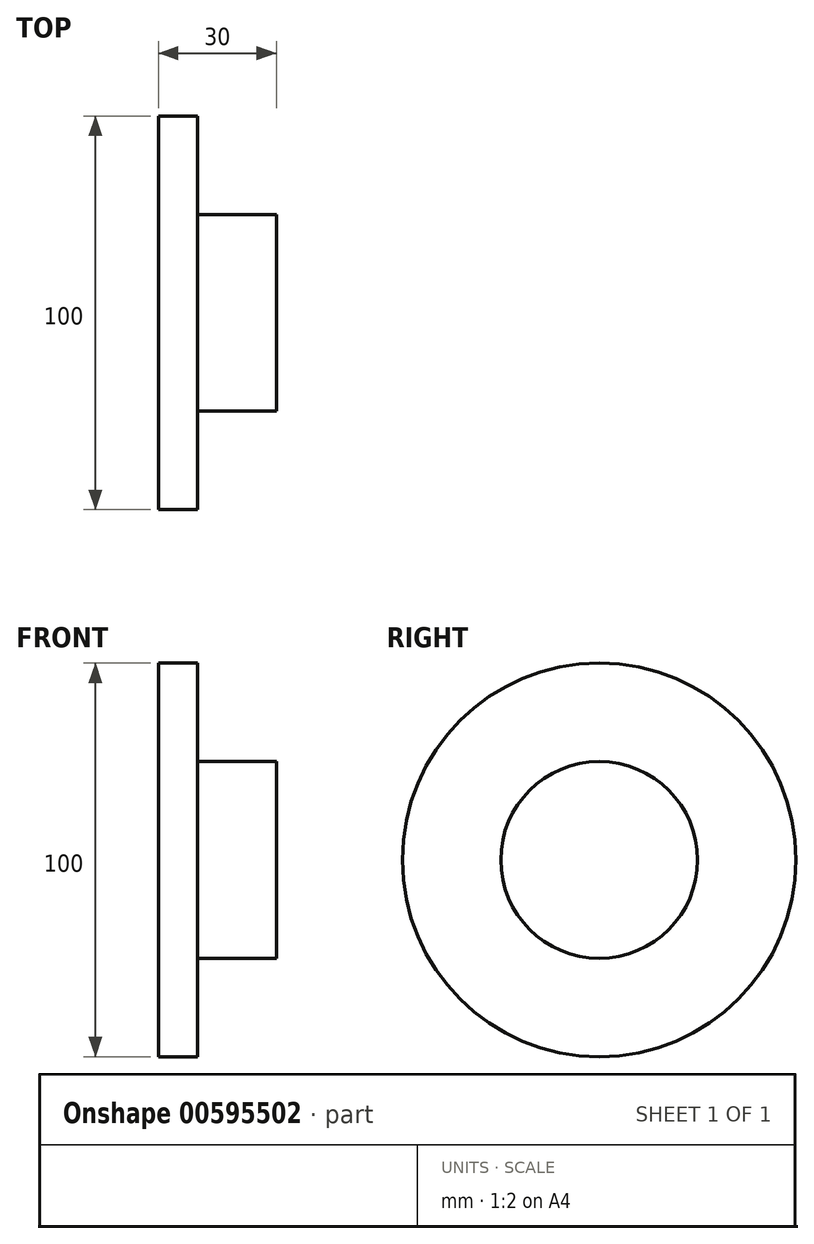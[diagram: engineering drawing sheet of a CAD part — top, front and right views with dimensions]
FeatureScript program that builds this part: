
annotation { "Feature Type Name" : "Feature", "Feature Type Description" : "" }
export const myFeature = defineFeature(function(context is Context, id is Id, definition is map)
    precondition{}
    {
        {
            var Q0;
            Q0=qCreatedBy(makeId("Front.planeOp"),FACE);
            var sketch = newSketch(context, id + "F0", { "sketchPlane" : qUnion([Q0])});
            skLineSegment(sketch, "E0", {"start": v(0, 0) * mm, "end": v(0, 50) * mm});
            skLineSegment(sketch, "E1", {"start": v(0, 50) * mm, "end": v(30, 50) * mm});
            skLineSegment(sketch, "E2", {"start": v(30, 50) * mm, "end": v(30, 25) * mm});
            skLineSegment(sketch, "E3", {"start": v(30, 25) * mm, "end": v(10, 25) * mm});
            skLineSegment(sketch, "E4", {"start": v(10, 25) * mm, "end": v(10, 0) * mm});
            skLineSegment(sketch, "E5", {"start": v(10, 0) * mm, "end": v(0, 0) * mm});
            skSolve(sketch);
        }
        {
            var Q0;
            Q0=makeQuery(id+"F0.imprint","IMPRINT",FACE,{"disambiguationData":[TD([[makeQuery(id+"F0.imprint","IMPRINT",EDGE,{"derivedFrom":sQuery(id+"F0.wireOp",EDGE,"E0")}),-1.0]])]});
            var Q1;
            Q1=sQuery(id+"F0.wireOp",EDGE,"E1");
            revolve(context, id + "F1", {"entities" : qUnion([Q0]), "axis" : qUnion([Q1]), "revolveType" : RevolveType.FULL});
        }
    });
